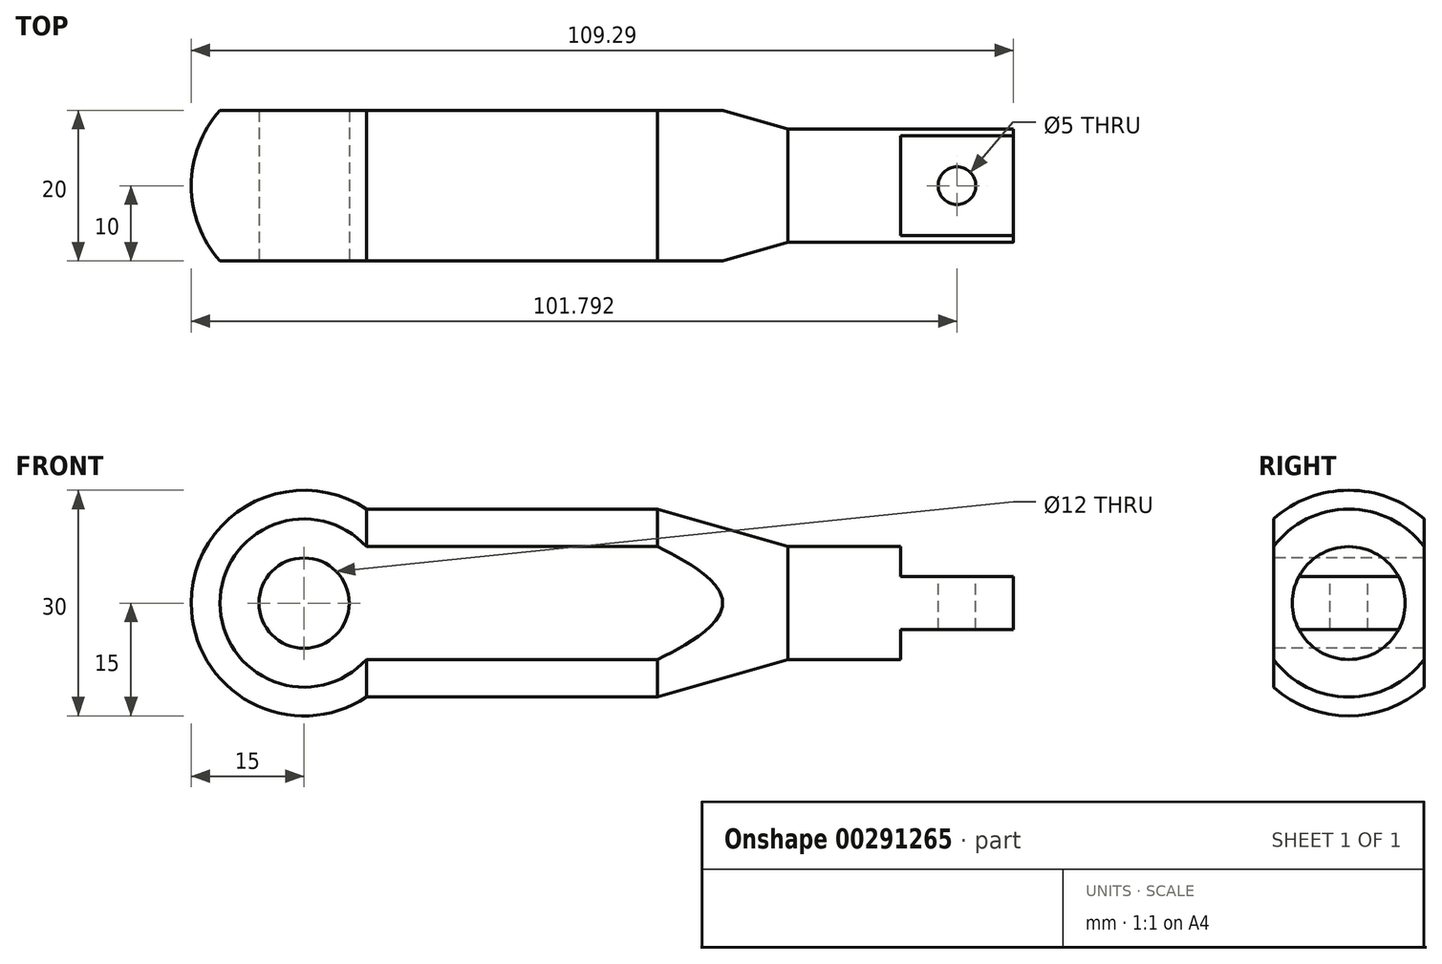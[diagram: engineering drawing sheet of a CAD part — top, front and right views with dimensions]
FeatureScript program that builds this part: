
annotation { "Feature Type Name" : "Feature", "Feature Type Description" : "" }
export const myFeature = defineFeature(function(context is Context, id is Id, definition is map)
    precondition{}
    {
        {
            var Q0;
            Q0=qCreatedBy(makeId("Front.planeOp"),FACE);
            var sketch = newSketch(context, id + "F0", { "sketchPlane" : qUnion([Q0])});
            skLineSegment(sketch, "E0", {"start": v(0, 0) * mm, "end": v(118.2, 0) * mm, "construction": true});
            skArc(sketch, "E1", {"start": v(-15, 0) * mm, "mid": v(-7.1, 13.22) * mm, "end": v(8.3, 12.5) * mm});
            skLineSegment(sketch, "E2", {"start": v(8.3, 12.5) * mm, "end": v(47, 12.5) * mm});
            skLineSegment(sketch, "E3", {"start": v(47, 12.5) * mm, "end": v(64.3, 7.5) * mm});
            skLineSegment(sketch, "E4", {"start": v(64.3, 7.5) * mm, "end": v(94.3, 7.5) * mm});
            skLineSegment(sketch, "E5", {"start": v(94.3, 7.5) * mm, "end": v(94.3, 0) * mm});
            skLineSegment(sketch, "E6", {"start": v(94.3, 0) * mm, "end": v(-15, 0) * mm});
            skSolve(sketch);
        }
        {
            var Q0;
            Q0 = qSketchRegion(id + "F0", true);
            var Q1;
            Q1=sQuery(id+"F0.wireOp",EDGE,"E6");
            revolve(context, id + "F1", {"entities" : qUnion([Q0]), "axis" : qUnion([Q1]), "revolveType" : RevolveType.FULL});
        }
        {
            var Q0;
            Q0=qCreatedBy(makeId("Front.planeOp"),FACE);
            var sketch = newSketch(context, id + "F2", { "sketchPlane" : qUnion([Q0])});
            skLineSegment(sketch, "E7", {"start": v(79.3, 7.5) * mm, "end": v(94.3, 7.5) * mm});
            skLineSegment(sketch, "E8.bottom", {"start": v(94.3, 7.5) * mm, "end": v(79.3, 7.5) * mm});
            skLineSegment(sketch, "E8.top", {"start": v(94.3, 3.5) * mm, "end": v(79.3, 3.5) * mm});
            skLineSegment(sketch, "E8.left", {"start": v(94.3, 7.5) * mm, "end": v(94.3, 3.5) * mm});
            skLineSegment(sketch, "E8.right", {"start": v(79.3, 7.5) * mm, "end": v(79.3, 3.5) * mm});
            skLineSegment(sketch, "E9", {"start": v(64.23, 0) * mm, "end": v(96.9, 0) * mm, "construction": true});
            skLineSegment(sketch, "E10.MirrorCS", {"start": v(79.3, -7.5) * mm, "end": v(94.3, -7.5) * mm});
            skLineSegment(sketch, "E11.MirrorCS", {"start": v(79.3, -7.5) * mm, "end": v(79.3, -3.5) * mm});
            skLineSegment(sketch, "E12.MirrorCS", {"start": v(94.3, -7.5) * mm, "end": v(94.3, -3.5) * mm});
            skLineSegment(sketch, "E13.MirrorCS", {"start": v(94.3, -3.5) * mm, "end": v(79.3, -3.5) * mm});
            skLineSegment(sketch, "E14.MirrorCS", {"start": v(94.3, -7.5) * mm, "end": v(79.3, -7.5) * mm});
            skSolve(sketch);
        }
        {
            var Q0;
            Q0 = qSketchRegion(id + "F2", true);
            extrude(context, id + "F3", {"entities" : qUnion([Q0]), "operationType" : NewBodyOperationType.REMOVE, "endBound" : BoundingType.THROUGH_ALL, "oppositeDirection" : true, "depth" : 25 * mm, "hasSecondDirection" : true, "secondDirectionBound" : SecondDirectionBoundingType.THROUGH_ALL, "secondDirectionOppositeDirection" : false, "secondDirectionDepth" : 25 * mm});
        }
        {
            var Q0;
            Q0=makeQuery(id+"F1.opRevolve","SWEPT_FACE",FACE,{"disambiguationData":[OSD([sQuery(id+"F0.wireOp",EDGE,"E5")])]});
            var sketch = newSketch(context, id + "F4", { "sketchPlane" : qUnion([Q0])});
            skCircle(sketch, "E15", {"center": v(0, 0) * mm, "radius": 15 * mm});
            skLineSegment(sketch, "E16", {"start": v(-10, 11.18) * mm, "end": v(-10, -11.18) * mm});
            skLineSegment(sketch, "E17", {"start": v(0, 0) * mm, "end": v(0, 16.88) * mm, "construction": true});
            skLineSegment(sketch, "E18.MirrorCS", {"start": v(10, 11.18) * mm, "end": v(10, -11.18) * mm});
            skSolve(sketch);
        }
        {
            var Q0;
            {var subQ0=sQuery(id+"F4.wireOp",EDGE,"E18.MirrorCS");Q0=makeQuery(id+"F4.imprint","IMPRINT",FACE,{"disambiguationData":[TD([[makeQuery(id+"F4.imprint","IMPRINT",EDGE,{"derivedFrom":subQ0}),1.0]])]});}
            var Q1;
            {var subQ0=sQuery(id+"F4.wireOp",EDGE,"E16");Q1=makeQuery(id+"F4.imprint","IMPRINT",FACE,{"disambiguationData":[TD([[makeQuery(id+"F4.imprint","IMPRINT",EDGE,{"derivedFrom":subQ0}),-1.0]])]});}
            extrude(context, id + "F5", {"entities" : qUnion([Q0, Q1]), "operationType" : NewBodyOperationType.REMOVE, "endBound" : BoundingType.THROUGH_ALL, "oppositeDirection" : true, "depth" : 25 * mm});
        }
        {
            var Q0;
            Q0=makeQuery(id+"F5.boolean.opBoolean","COPY",FACE,{"derivedFrom":makeQuery(id+"F5.opExtrude","SWEPT_FACE",FACE,{"disambiguationData":[OSD([sQuery(id+"F4.wireOp",EDGE,"E16")])]})});
            var sketch = newSketch(context, id + "F6", { "sketchPlane" : qUnion([Q0])});
            skCircle(sketch, "E19", {"center": v(0, 0) * mm, "radius": 6 * mm});
            skSolve(sketch);
        }
        {
            var Q0;
            Q0 = qSketchRegion(id + "F6", true);
            extrude(context, id + "F7", {"entities" : qUnion([Q0]), "operationType" : NewBodyOperationType.REMOVE, "endBound" : BoundingType.THROUGH_ALL, "oppositeDirection" : true, "depth" : 25 * mm});
        }
        {
            var Q0;
            Q0=makeQuery(id+"F3.boolean.opBoolean","COPY",FACE,{"derivedFrom":makeQuery(id+"F3.opExtrude","SWEPT_FACE",FACE,{"disambiguationData":[OSD([sQuery(id+"F2.wireOp",EDGE,"E8.top")])]})});
            var sketch = newSketch(context, id + "F8", { "sketchPlane" : qUnion([Q0])});
            skCircle(sketch, "E20", {"center": v(86.8, 0) * mm, "radius": 2.5 * mm});
            skSolve(sketch);
        }
        {
            var Q0;
            Q0 = qSketchRegion(id + "F8", true);
            extrude(context, id + "F9", {"entities" : qUnion([Q0]), "operationType" : NewBodyOperationType.REMOVE, "endBound" : BoundingType.THROUGH_ALL, "oppositeDirection" : true, "depth" : 25 * mm});
        }
    });
